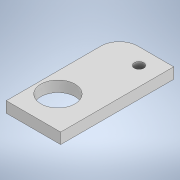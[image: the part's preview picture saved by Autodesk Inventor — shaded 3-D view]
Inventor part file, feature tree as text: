
AUTODESK INVENTOR PART (.ipt)
format: ipt  version: 2021 (Build 250183000, 183)  size: 111,616 bytes
history: native  units: mm
features: extrude x1, sketch x1
ambient origin geometry x8: Origin, YZ Plane, XZ Plane, XY Plane, X Axis, Y Axis, Z Axis, Center Point
bodies: Solid1 (feature_tree)
feature tree (2):
  extrude  "Extrusion1"  Depth=52.0mm
  sketch  "Sketch1"  dims[d0=25.0mm d1=52.0mm d2=8.5mm d3=15.75mm d4=4.4mm d5=16.5mm d6=7.45mm d7=20.0mm d8=9.2mm d9=30.0mm d10=5.0mm d11=0.0mm]
